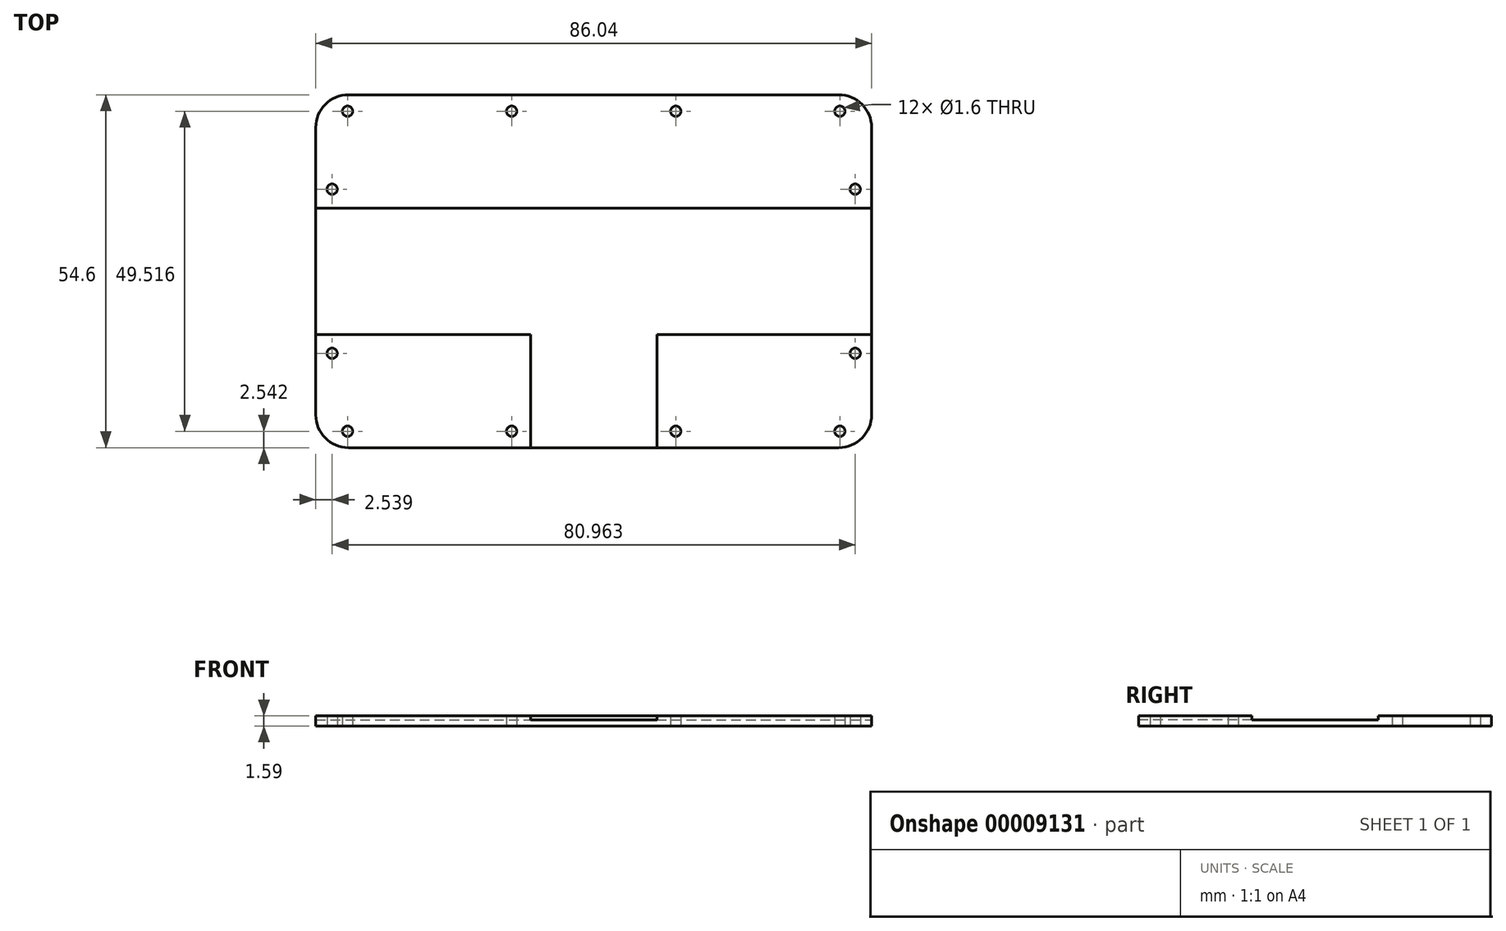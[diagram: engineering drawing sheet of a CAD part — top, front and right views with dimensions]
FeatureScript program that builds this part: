
annotation { "Feature Type Name" : "Feature", "Feature Type Description" : "" }
export const myFeature = defineFeature(function(context is Context, id is Id, definition is map)
    precondition{}
    {
        {
            var Q0;
            Q0=qCreatedBy(makeId("Top.planeOp"),FACE);
            var sketch = newSketch(context, id + "F0", { "sketchPlane" : qUnion([Q0])});
            skLineSegment(sketch, "E0.bottom", {"start": v(-43.02, 27.3) * mm, "end": v(43.02, 27.3) * mm});
            skLineSegment(sketch, "E0.top", {"start": v(-43.02, -27.3) * mm, "end": v(43.02, -27.3) * mm});
            skLineSegment(sketch, "E0.left", {"start": v(-43.02, 27.3) * mm, "end": v(-43.02, -27.3) * mm});
            skLineSegment(sketch, "E0.right", {"start": v(43.02, 27.3) * mm, "end": v(43.02, -27.3) * mm});
            skLineSegment(sketch, "E1", {"start": v(0, 28.85) * mm, "end": v(0, -30.48) * mm, "construction": true});
            skLineSegment(sketch, "E2", {"start": v(-35.92, 0) * mm, "end": v(38.92, 0) * mm, "construction": true});
            skCircle(sketch, "E3", {"center": v(-38.1, 24.76) * mm, "radius": 0.8 * mm});
            skCircle(sketch, "E4.0.MirrorC", {"center": v(-38.1, -24.76) * mm, "radius": 0.8 * mm});
            skCircle(sketch, "E5.1.0.0", {"center": v(-12.7, 24.76) * mm, "radius": 0.8 * mm});
            skCircle(sketch, "E5.2.0.0", {"center": v(12.7, 24.76) * mm, "radius": 0.8 * mm});
            skCircle(sketch, "E5.3.0.0", {"center": v(38.1, 24.76) * mm, "radius": 0.8 * mm});
            skLineSegment(sketch, "E5.direction1", {"start": v(-38.1, 24.76) * mm, "end": v(-12.7, 24.76) * mm, "construction": true});
            skCircle(sketch, "E6.1.0.0", {"center": v(-12.7, -24.76) * mm, "radius": 0.8 * mm});
            skCircle(sketch, "E6.2.0.0", {"center": v(12.7, -24.76) * mm, "radius": 0.8 * mm});
            skCircle(sketch, "E6.3.0.0", {"center": v(38.1, -24.76) * mm, "radius": 0.8 * mm});
            skLineSegment(sketch, "E6.direction1", {"start": v(-38.1, -24.76) * mm, "end": v(-12.7, -24.76) * mm, "construction": true});
            skCircle(sketch, "E7", {"center": v(-40.48, 12.7) * mm, "radius": 0.8 * mm});
            skCircle(sketch, "E8.0.1.0", {"center": v(-40.48, -12.7) * mm, "radius": 0.8 * mm});
            skLineSegment(sketch, "E8.direction1", {"start": v(-40.48, 12.7) * mm, "end": v(-21.14, 12.74) * mm, "construction": true});
            skLineSegment(sketch, "E8.direction2", {"start": v(-40.48, 12.7) * mm, "end": v(-40.48, -12.7) * mm, "construction": true});
            skCircle(sketch, "E9.0.MirrorC", {"center": v(40.48, -12.7) * mm, "radius": 0.8 * mm});
            skCircle(sketch, "E9.1.MirrorC", {"center": v(40.48, 12.7) * mm, "radius": 0.8 * mm});
            skSolve(sketch);
        }
        {
            var Q0;
            Q0=makeQuery(id+"F0.imprint","IMPRINT",FACE,{"disambiguationData":[TD([[makeQuery(id+"F0.imprint","IMPRINT",EDGE,{"derivedFrom":sQuery(id+"F0.wireOp",EDGE,"E0.bottom")}),-1.0]])]});
            extrude(context, id + "F1", {"entities" : qUnion([Q0]), "depth" : 1.59 * mm});
        }
        {
            var Q0;
            Q0=makeQuery(id+"F1.opExtrude","SWEPT_EDGE",EDGE,{"disambiguationData":[OSD([sQuery(id+"F0.wireOp",EDGE,"E0.bottom"),sQuery(id+"F0.wireOp",EDGE,"E0.left")])]});
            var Q1;
            Q1=makeQuery(id+"F1.opExtrude","SWEPT_EDGE",EDGE,{"disambiguationData":[OSD([sQuery(id+"F0.wireOp",EDGE,"E0.top"),sQuery(id+"F0.wireOp",EDGE,"E0.left")])]});
            var Q2;
            Q2=makeQuery(id+"F1.opExtrude","SWEPT_EDGE",EDGE,{"disambiguationData":[OSD([sQuery(id+"F0.wireOp",EDGE,"E0.top"),sQuery(id+"F0.wireOp",EDGE,"E0.right")])]});
            var Q3;
            Q3=makeQuery(id+"F1.opExtrude","SWEPT_EDGE",EDGE,{"disambiguationData":[OSD([sQuery(id+"F0.wireOp",EDGE,"E0.bottom"),sQuery(id+"F0.wireOp",EDGE,"E0.right")])]});
            fillet(context, id + "F2", {"entities" : qUnion([Q0, Q1, Q2, Q3]), "radius" : 5.08 * mm, "tangentPropagation" : true, "allowEdgeOverflow" : false});
        }
        {
            var Q0;
            Q0=makeQuery(id+"F1.opExtrude","CAP_FACE",FACE,{"disambiguationData":[OSD([sQuery(id+"F0.wireOp",EDGE,"E0.bottom"),sQuery(id+"F0.wireOp",EDGE,"E0.top"),sQuery(id+"F0.wireOp",EDGE,"E0.left"),sQuery(id+"F0.wireOp",EDGE,"E0.right"),sQuery(id+"F0.wireOp",EDGE,"b0c5e1c4-3e76-44be-b8ab-dbbe46599de7.bottom"),sQuery(id+"F0.wireOp",EDGE,"b0c5e1c4-3e76-44be-b8ab-dbbe46599de7.top"),sQuery(id+"F0.wireOp",EDGE,"b0c5e1c4-3e76-44be-b8ab-dbbe46599de7.left"),sQuery(id+"F0.wireOp",EDGE,"b0c5e1c4-3e76-44be-b8ab-dbbe46599de7.right"),sQuery(id+"F0.wireOp",EDGE,"E3"),sQuery(id+"F0.wireOp",EDGE,"E4.0.MirrorC"),sQuery(id+"F0.wireOp",EDGE,"E5.1.0.0"),sQuery(id+"F0.wireOp",EDGE,"E5.2.0.0"),sQuery(id+"F0.wireOp",EDGE,"E5.3.0.0"),sQuery(id+"F0.wireOp",EDGE,"E6.1.0.0"),sQuery(id+"F0.wireOp",EDGE,"E6.2.0.0"),sQuery(id+"F0.wireOp",EDGE,"E6.3.0.0"),sQuery(id+"F0.wireOp",EDGE,"E7"),sQuery(id+"F0.wireOp",EDGE,"E8.0.1.0"),sQuery(id+"F0.wireOp",EDGE,"E9.1.MirrorC"),sQuery(id+"F0.wireOp",EDGE,"E9.0.MirrorC")])],"isStart":false});
            var sketch = newSketch(context, id + "F3", { "sketchPlane" : qUnion([Q0])});
            skLineSegment(sketch, "E10", {"start": v(-9.78, -9.78) * mm, "end": v(-9.78, -27.3) * mm});
            skLineSegment(sketch, "E11", {"start": v(9.78, -9.78) * mm, "end": v(9.78, -27.3) * mm});
            skLineSegment(sketch, "E12.0", {"start": v(-43.02, 9.78) * mm, "end": v(-43.02, -9.78) * mm});
            skLineSegment(sketch, "E13.0", {"start": v(-9.78, -27.3) * mm, "end": v(9.78, -27.3) * mm});
            skLineSegment(sketch, "E14.trimOffspring", {"start": v(-43.02, 9.78) * mm, "end": v(43.02, 9.78) * mm});
            skLineSegment(sketch, "E15.trimOffspring", {"start": v(-43.02, -9.78) * mm, "end": v(-9.78, -9.78) * mm});
            skLineSegment(sketch, "E16.0", {"start": v(43.02, 9.8) * mm, "end": v(43.02, -9.78) * mm});
            skLineSegment(sketch, "E17.trimOffspring", {"start": v(9.78, -9.78) * mm, "end": v(43.02, -9.78) * mm});
            skSolve(sketch);
        }
        {
            var Q0;
            Q0=qSketchRegion(id+"F3",true);
            extrude(context, id + "F4", {"entities" : qUnion([Q0]), "operationType" : NewBodyOperationType.REMOVE, "oppositeDirection" : true, "depth" : 0.64 * mm});
        }
    });
